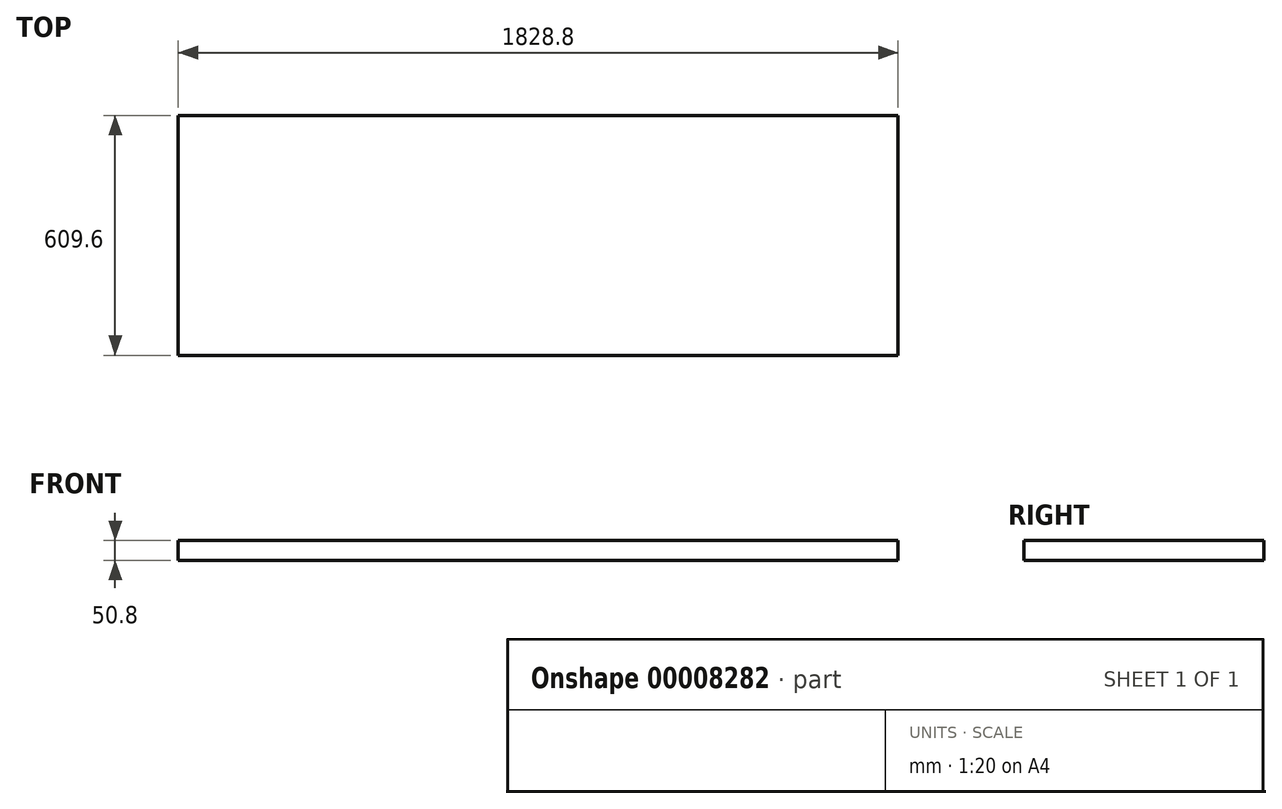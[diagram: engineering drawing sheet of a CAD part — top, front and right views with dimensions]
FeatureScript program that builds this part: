
annotation { "Feature Type Name" : "Feature", "Feature Type Description" : "" }
export const myFeature = defineFeature(function(context is Context, id is Id, definition is map)
    precondition{}
    {
        {
            var Q0;
            Q0=qCreatedBy(makeId("Top.planeOp"),FACE);
            var sketch = newSketch(context, id + "F0", { "sketchPlane" : qUnion([Q0])});
            skLineSegment(sketch, "E0.bottom", {"start": v(0, -397.87) * mm, "end": v(1828.8, -397.87) * mm});
            skLineSegment(sketch, "E0.top", {"start": v(0, -1007.47) * mm, "end": v(1828.8, -1007.47) * mm});
            skLineSegment(sketch, "E0.left", {"start": v(0, -397.87) * mm, "end": v(0, -1007.47) * mm});
            skLineSegment(sketch, "E0.right", {"start": v(1828.8, -397.87) * mm, "end": v(1828.8, -1007.47) * mm});
            skSolve(sketch);
        }
        {
            var Q0;
            Q0=makeQuery(id+"F0.imprint","IMPRINT",FACE,{"disambiguationData":[TD([[makeQuery(id+"F0.imprint","IMPRINT",EDGE,{"derivedFrom":sQuery(id+"F0.wireOp",EDGE,"E0.bottom")}),-1.0]])]});
            extrude(context, id + "F1", {"entities" : qUnion([Q0]), "depth" : 50.8 * mm});
        }
    });
